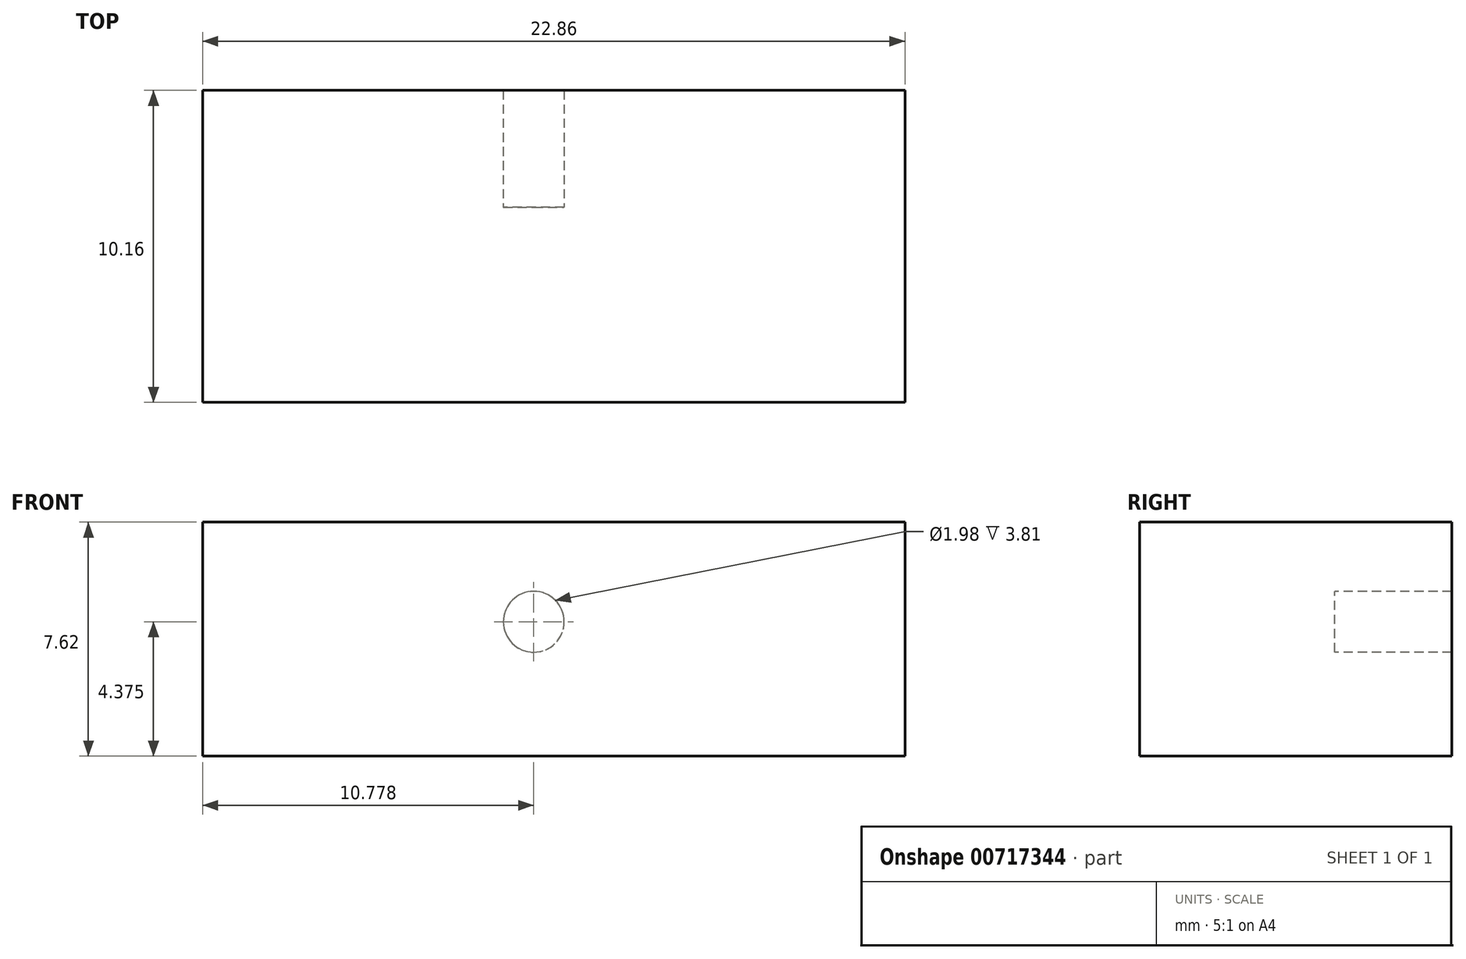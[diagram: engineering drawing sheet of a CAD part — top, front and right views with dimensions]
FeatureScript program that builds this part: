
annotation { "Feature Type Name" : "Feature", "Feature Type Description" : "" }
export const myFeature = defineFeature(function(context is Context, id is Id, definition is map)
    precondition{}
    {
        {
            var Q0;
            Q0=qCreatedBy(makeId("Top.planeOp"),FACE);
            var sketch = newSketch(context, id + "F0", { "sketchPlane" : qUnion([Q0])});
            skLineSegment(sketch, "E0.bottom", {"start": v(-39.74, -10.16) * mm, "end": v(-16.88, -10.16) * mm});
            skLineSegment(sketch, "E0.top", {"start": v(-39.74, 0) * mm, "end": v(-16.88, 0) * mm});
            skLineSegment(sketch, "E0.left", {"start": v(-39.74, -10.16) * mm, "end": v(-39.74, 0) * mm});
            skLineSegment(sketch, "E0.right", {"start": v(-16.88, -10.16) * mm, "end": v(-16.88, 0) * mm});
            skSolve(sketch);
        }
        {
            var Q0;
            Q0=makeQuery(id+"F0.imprint","IMPRINT",FACE,{"disambiguationData":[TD([[makeQuery(id+"F0.imprint","IMPRINT",EDGE,{"derivedFrom":sQuery(id+"F0.wireOp",EDGE,"E0.bottom")}),1.0]])]});
            extrude(context, id + "F1", {"entities" : qUnion([Q0]), "depth" : 7.62 * mm, "offsetDistance" : 25.4 * mm});
        }
        {
            var Q0;
            Q0=qCreatedBy(makeId("Front.planeOp"),FACE);
            var sketch = newSketch(context, id + "F2", { "sketchPlane" : qUnion([Q0])});
            skCircle(sketch, "E1", {"center": v(-28.96, 4.38) * mm, "radius": 1 * mm});
            skSolve(sketch);
        }
        {
            var Q0;
            Q0=makeQuery(id+"F2.imprint","IMPRINT",FACE,{"disambiguationData":[TD([[makeQuery(id+"F2.imprint","IMPRINT",EDGE,{"derivedFrom":sQuery(id+"F2.wireOp",EDGE,"E1")}),1.0]])]});
            extrude(context, id + "F3", {"entities" : qUnion([Q0]), "operationType" : NewBodyOperationType.REMOVE, "endBound" : BoundingType.SYMMETRIC, "oppositeDirection" : true, "depth" : 7.62 * mm, "offsetDistance" : 25.4 * mm});
        }
    });
